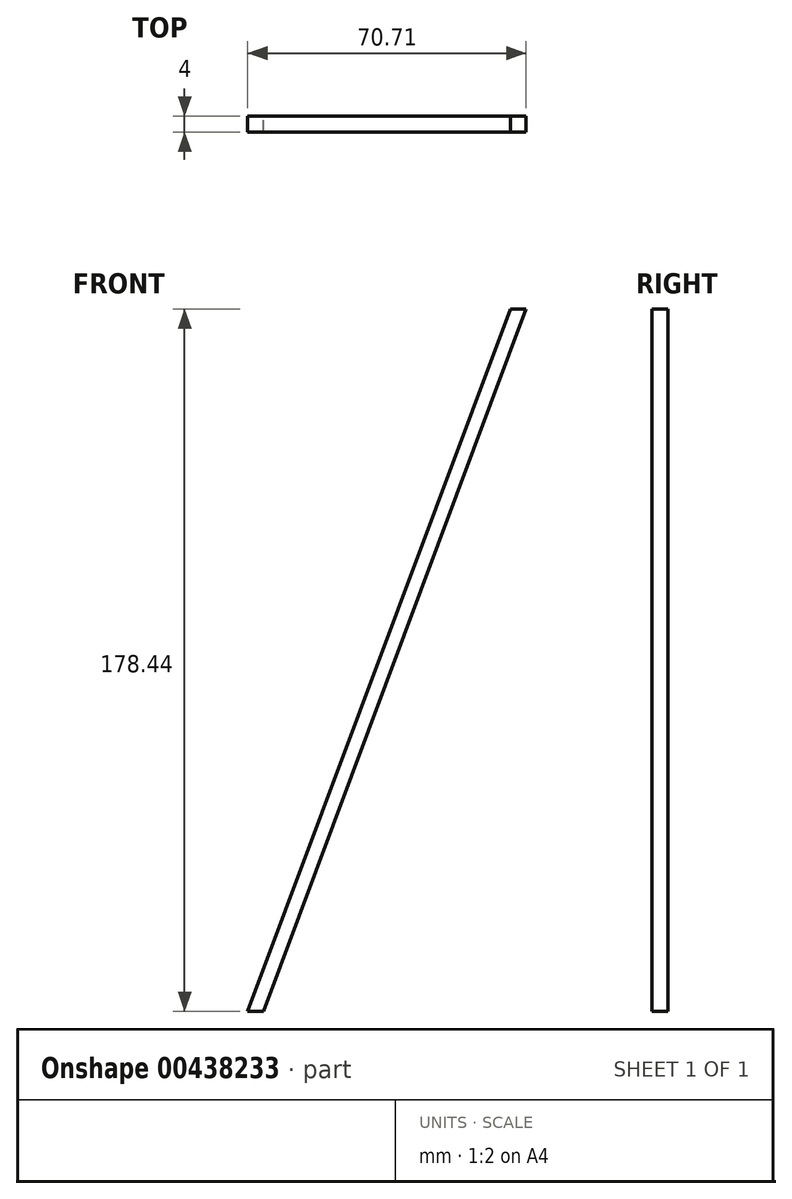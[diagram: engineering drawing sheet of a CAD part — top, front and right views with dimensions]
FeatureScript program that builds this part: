
annotation { "Feature Type Name" : "Feature", "Feature Type Description" : "" }
export const myFeature = defineFeature(function(context is Context, id is Id, definition is map)
    precondition{}
    {
        {
            var Q0;
            Q0=qCreatedBy(makeId("Front.planeOp"),FACE);
            var sketch = newSketch(context, id + "F0", { "sketchPlane" : qUnion([Q0])});
            skLineSegment(sketch, "E0", {"start": v(-23.07, 31.92) * mm, "end": v(-19.07, 31.92) * mm});
            skLineSegment(sketch, "E1", {"start": v(-19.07, 31.92) * mm, "end": v(47.64, 210.36) * mm});
            skLineSegment(sketch, "E2", {"start": v(47.64, 210.36) * mm, "end": v(43.64, 210.36) * mm});
            skLineSegment(sketch, "E3", {"start": v(43.64, 210.36) * mm, "end": v(-23.07, 31.92) * mm});
            skSolve(sketch);
        }
        {
            var Q0;
            Q0=makeQuery(id+"F0.imprint","IMPRINT",FACE,{"disambiguationData":[TD([[makeQuery(id+"F0.imprint","IMPRINT",EDGE,{"derivedFrom":sQuery(id+"F0.wireOp",EDGE,"E0")}),1.0]])]});
            extrude(context, id + "F1", {"entities" : qUnion([Q0]), "depth" : 4 * mm});
        }
    });
